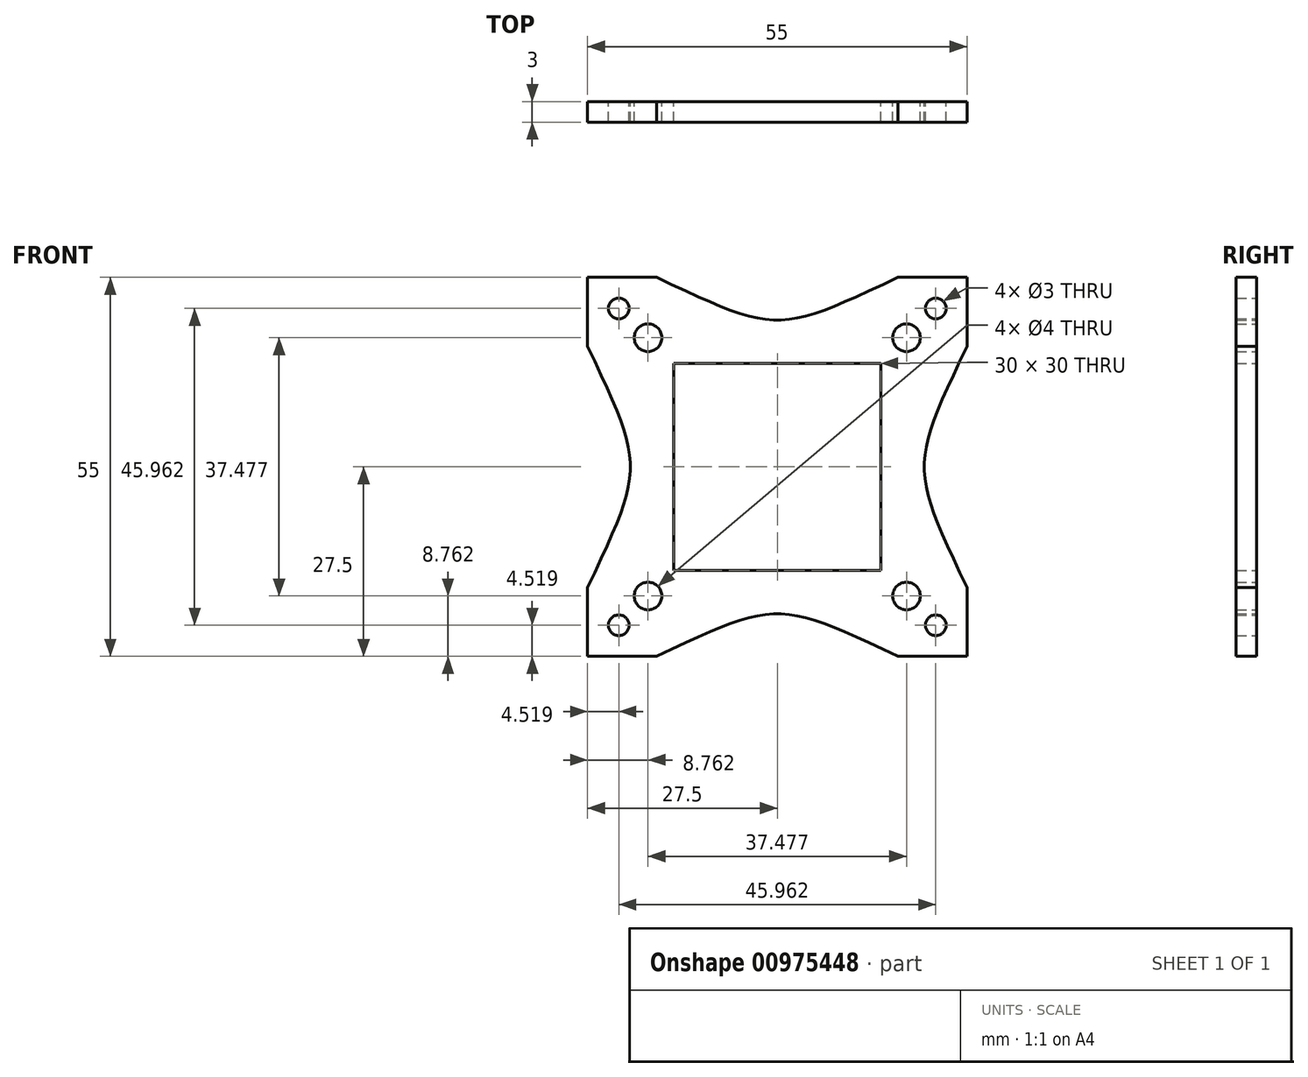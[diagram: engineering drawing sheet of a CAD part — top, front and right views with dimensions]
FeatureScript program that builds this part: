
annotation { "Feature Type Name" : "Feature", "Feature Type Description" : "" }
export const myFeature = defineFeature(function(context is Context, id is Id, definition is map)
    precondition{}
    {
        {
            var Q0;
            Q0=qCreatedBy(makeId("Front.planeOp"),FACE);
            var sketch = newSketch(context, id + "F0", { "sketchPlane" : qUnion([Q0])});
            skPoint(sketch, "E0.middle", {"position": v(0, 0) * mm});
            skCircle(sketch, "E1", {"center": v(-22.98, 22.98) * mm, "radius": 1.5 * mm});
            skCircle(sketch, "E2", {"center": v(22.98, 22.98) * mm, "radius": 1.5 * mm});
            skCircle(sketch, "E3", {"center": v(22.98, -22.98) * mm, "radius": 1.5 * mm});
            skCircle(sketch, "E4", {"center": v(-22.98, -22.98) * mm, "radius": 1.5 * mm});
            skLineSegment(sketch, "E5.bottom", {"start": v(27.5, 27.5) * mm, "end": v(17.5, 27.5) * mm});
            skLineSegment(sketch, "E5.top", {"start": v(27.5, -27.5) * mm, "end": v(17.5, -27.5) * mm});
            skLineSegment(sketch, "E5.left", {"start": v(27.5, 27.5) * mm, "end": v(27.5, 17.5) * mm});
            skLineSegment(sketch, "E5.right", {"start": v(-27.5, 27.5) * mm, "end": v(-27.5, 17.5) * mm});
            skFitSpline(sketch, "E6", {"points": [v(-27.5, 17.5) * mm, v(-27.5, -17.5) * mm], "startDerivative": vector(24.77, -52.5) * mm, "endDerivative": vector(-24.77, -52.5) * mm});
            skFitSpline(sketch, "E7", {"points": [v(27.5, -17.5) * mm, v(27.5, 17.5) * mm], "startDerivative": vector(-24.77, 52.5) * mm, "endDerivative": vector(24.77, 52.5) * mm});
            skLineSegment(sketch, "E8.bottom", {"start": v(-131.23, 54.42) * mm, "end": v(-76.23, 54.42) * mm});
            skLineSegment(sketch, "E8.left", {"start": v(-131.23, 54.42) * mm, "end": v(-131.23, 19.42) * mm});
            skLineSegment(sketch, "E8.right", {"start": v(-76.23, 54.42) * mm, "end": v(-76.23, 19.42) * mm});
            skFitSpline(sketch, "E9", {"points": [v(17.5, 27.5) * mm, v(-17.5, 27.5) * mm], "startDerivative": vector(-52.5, -24.77) * mm, "endDerivative": vector(-52.5, 24.77) * mm});
            skFitSpline(sketch, "E10", {"points": [v(-17.5, -27.5) * mm, v(17.5, -27.5) * mm], "startDerivative": vector(52.5, 24.77) * mm, "endDerivative": vector(52.5, -24.77) * mm});
            skCircle(sketch, "E11", {"center": v(-18.74, 18.74) * mm, "radius": 2 * mm});
            skCircle(sketch, "E12.1.0", {"center": v(-18.74, -18.74) * mm, "radius": 2 * mm});
            skCircle(sketch, "E12.2.0", {"center": v(18.74, -18.74) * mm, "radius": 2 * mm});
            skCircle(sketch, "E12.3.0", {"center": v(18.74, 18.74) * mm, "radius": 2 * mm});
            skLineSegment(sketch, "E13.trimOffspring", {"start": v(-17.5, 27.5) * mm, "end": v(-27.5, 27.5) * mm});
            skLineSegment(sketch, "E14.trimOffspring", {"start": v(27.5, -17.5) * mm, "end": v(27.5, -27.5) * mm});
            skLineSegment(sketch, "E15.trimOffspring", {"start": v(-27.5, -17.5) * mm, "end": v(-27.5, -27.5) * mm});
            skLineSegment(sketch, "E16.trimOffspring", {"start": v(-17.5, -27.5) * mm, "end": v(-27.5, -27.5) * mm});
            skLineSegment(sketch, "E17.bottom", {"start": v(15, 15) * mm, "end": v(-15, 15) * mm});
            skLineSegment(sketch, "E17.top", {"start": v(15, -15) * mm, "end": v(-15, -15) * mm});
            skLineSegment(sketch, "E17.left", {"start": v(15, 15) * mm, "end": v(15, -15) * mm});
            skLineSegment(sketch, "E17.right", {"start": v(-15, 15) * mm, "end": v(-15, -15) * mm});
            skSolve(sketch);
        }
        {
            var Q0;
            Q0=makeQuery(id+"F0.imprint","IMPRINT",FACE,{"disambiguationData":[TD([[makeQuery(id+"F0.imprint","IMPRINT",EDGE,{"derivedFrom":sQuery(id+"F0.wireOp",EDGE,"E1")}),-1.0]])]});
            extrude(context, id + "F1", {"entities" : qUnion([Q0]), "depth" : 3 * mm, "offsetDistance" : 25 * mm});
        }
    });
